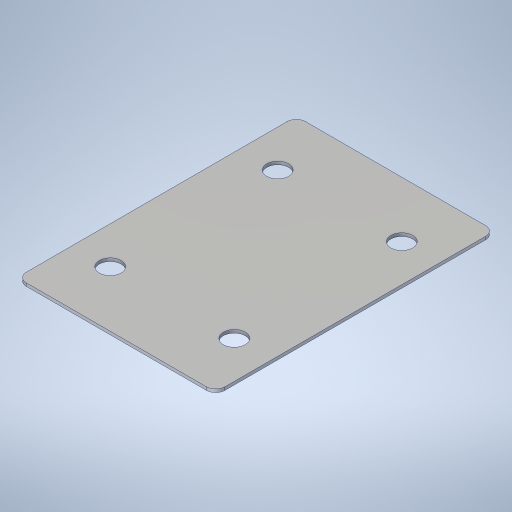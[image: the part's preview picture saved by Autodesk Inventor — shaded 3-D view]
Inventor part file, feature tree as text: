
AUTODESK INVENTOR PART (.ipt)
format: ipt  version: 2023.4 (Build 274418000, 418)  size: 233,472 bytes
history: native  units: in
note: dims shown in document units (in); Inventor stores cm internally (conversion verified against a paired STEP export)
features: sketch x2, extrude x1, hole x1, fillet x1
ambient origin geometry x8: Origin, YZ Plane, XZ Plane, XY Plane, X Axis, Y Axis, Z Axis, Center Point
bodies: Solid1 (feature_tree)
feature tree (5):
  extrude  "Extrusion1"  Depth=11.25in
  hole  "Hole1"  [1 undecoded]
  fillet  "Fillet1"  Radius=2.5in
  sketch  "Sketch1"  dims[d0=8.0in d1=11.25in]
  sketch  "Sketch2"  dims[d2=0.125in d3=0.0in d4=3.375in d5=2.5in d6=0.875in d7=0.328in d8=0.375in d9=0.25in d10=0.5635in d11=1.0in d12=0.8108in d13=0.375in]
note: 1 required parameter value undecoded (feature->parameter linkage not recoverable at this tier; creation-order binding heuristic only, values carry confidence <= 0.55)
